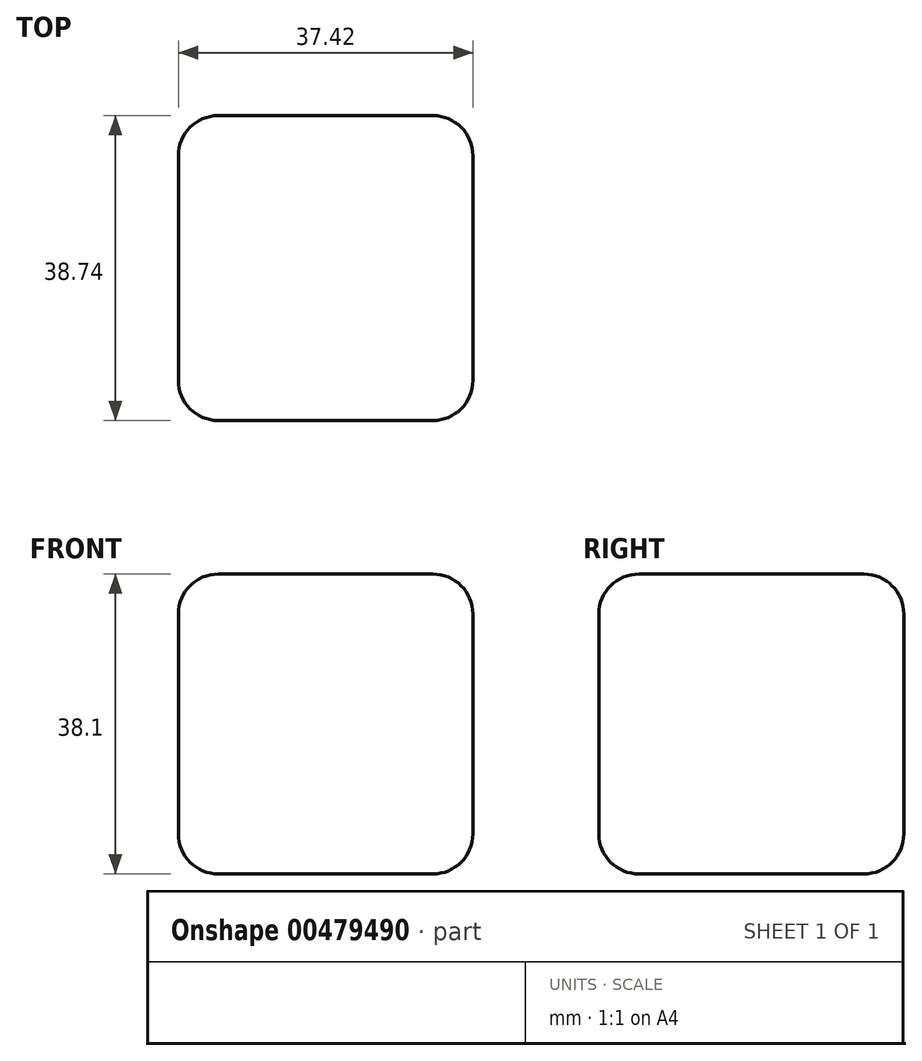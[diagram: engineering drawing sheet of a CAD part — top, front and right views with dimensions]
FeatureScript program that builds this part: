
annotation { "Feature Type Name" : "Feature", "Feature Type Description" : "" }
export const myFeature = defineFeature(function(context is Context, id is Id, definition is map)
    precondition{}
    {
        {
            var Q0;
            Q0=qCreatedBy(makeId("Top.planeOp"),FACE);
            var sketch = newSketch(context, id + "F0", { "sketchPlane" : qUnion([Q0])});
            skLineSegment(sketch, "E0.bottom", {"start": v(18.7, 19.37) * mm, "end": v(-18.7, 19.37) * mm});
            skLineSegment(sketch, "E0.top", {"start": v(18.7, -19.37) * mm, "end": v(-18.7, -19.37) * mm});
            skLineSegment(sketch, "E0.left", {"start": v(18.7, 19.37) * mm, "end": v(18.7, -19.37) * mm});
            skLineSegment(sketch, "E0.right", {"start": v(-18.7, 19.37) * mm, "end": v(-18.7, -19.37) * mm});
            skPoint(sketch, "E0.middle", {"position": v(0, 0) * mm});
            skSolve(sketch);
        }
        {
            var Q0;
            Q0=makeQuery(id+"F0.imprint","IMPRINT",FACE,{"disambiguationData":[TD([[makeQuery(id+"F0.imprint","IMPRINT",EDGE,{"derivedFrom":sQuery(id+"F0.wireOp",EDGE,"E0.bottom")}),1.0]])]});
            extrude(context, id + "F1", {"entities" : qUnion([Q0]), "depth" : 38.1 * mm});
        }
        {
            var Q0;
            Q0=makeQuery(id+"F1.opExtrude","SWEPT_EDGE",EDGE,{"disambiguationData":[OSD([sQuery(id+"F0.wireOp",EDGE,"E0.top"),sQuery(id+"F0.wireOp",EDGE,"E0.left")])]});
            fillet(context, id + "F2", {"entities" : qUnion([Q0]), "radius" : 5.08 * mm, "tangentPropagation" : true, "allowEdgeOverflow" : false});
        }
        {
            var Q0;
            Q0=makeQuery(id+"F1.opExtrude","SWEPT_EDGE",EDGE,{"disambiguationData":[OSD([sQuery(id+"F0.wireOp",EDGE,"E0.top"),sQuery(id+"F0.wireOp",EDGE,"E0.right")])]});
            fillet(context, id + "F3", {"entities" : qUnion([Q0]), "radius" : 5.08 * mm, "tangentPropagation" : true, "allowEdgeOverflow" : false});
        }
        {
            var Q0;
            Q0=makeQuery(id+"F1.opExtrude","SWEPT_EDGE",EDGE,{"disambiguationData":[OSD([sQuery(id+"F0.wireOp",EDGE,"E0.bottom"),sQuery(id+"F0.wireOp",EDGE,"E0.right")])]});
            fillet(context, id + "F4", {"entities" : qUnion([Q0]), "radius" : 5.08 * mm, "tangentPropagation" : true, "allowEdgeOverflow" : false});
        }
        {
            var Q0;
            Q0=makeQuery(id+"F1.opExtrude","SWEPT_EDGE",EDGE,{"disambiguationData":[OSD([sQuery(id+"F0.wireOp",EDGE,"E0.bottom"),sQuery(id+"F0.wireOp",EDGE,"E0.left")])]});
            fillet(context, id + "F5", {"entities" : qUnion([Q0]), "radius" : 5.08 * mm, "tangentPropagation" : true, "allowEdgeOverflow" : false});
        }
        {
            var Q0;
            Q0=makeQuery(id+"F1.opExtrude","CAP_EDGE",EDGE,{"disambiguationData":[OSD([sQuery(id+"F0.wireOp",EDGE,"E0.bottom")])],"isStart":false});
            fillet(context, id + "F6", {"entities" : qUnion([Q0]), "radius" : 5.08 * mm, "tangentPropagation" : true, "allowEdgeOverflow" : false});
        }
        {
            var Q0;
            Q0=makeQuery(id+"F1.opExtrude","CAP_EDGE",EDGE,{"disambiguationData":[OSD([sQuery(id+"F0.wireOp",EDGE,"E0.top")])],"isStart":true});
            fillet(context, id + "F7", {"entities" : qUnion([Q0]), "radius" : 5.08 * mm, "tangentPropagation" : true, "allowEdgeOverflow" : false});
        }
        {
            var Q0;
            Q0=qCreatedBy(makeId("Top.planeOp"),FACE);
            var sketch = newSketch(context, id + "F8", { "sketchPlane" : qUnion([Q0])});
            skCircle(sketch, "E1", {"center": v(-33.96, 60.33) * mm, "radius": 3.93 * mm});
            skSolve(sketch);
        }
        {
            var Q0;
            Q0=sQuery(id+"F8.wireOp",EDGE,"E1");
            extrude(context, id + "F9", {"bodyType" : ToolBodyType.SURFACE, "surfaceEntities" : qUnion([Q0]), "depth" : 0.25 * mm});
        }
    });
